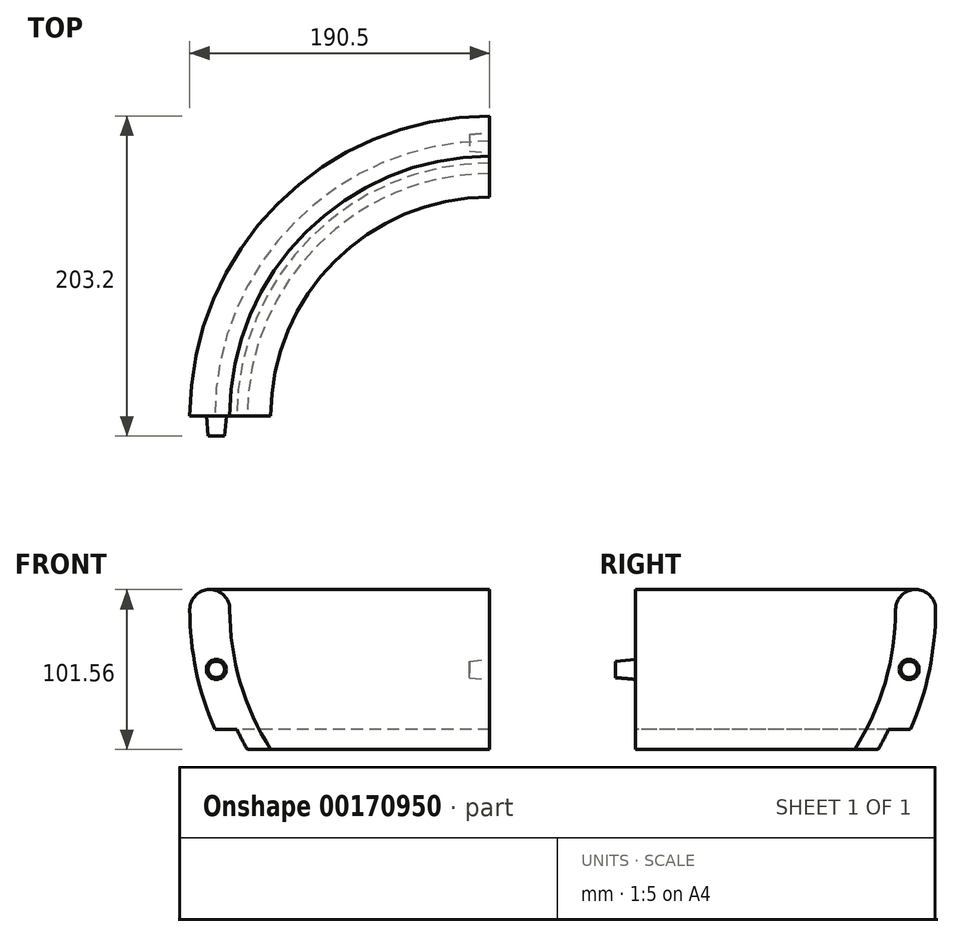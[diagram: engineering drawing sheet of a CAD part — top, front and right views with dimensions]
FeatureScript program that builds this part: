
annotation { "Feature Type Name" : "Feature", "Feature Type Description" : "" }
export const myFeature = defineFeature(function(context is Context, id is Id, definition is map)
    precondition{}
    {
        {
            var Q0;
            Q0=qCreatedBy(makeId("Front.planeOp"),FACE);
            var sketch = newSketch(context, id + "F0", { "sketchPlane" : qUnion([Q0])});
            skLineSegment(sketch, "E0", {"start": v(0, 0) * mm, "end": v(-165.1, 0) * mm});
            skLineSegment(sketch, "E1", {"start": v(0, 0) * mm, "end": v(0, -76.2) * mm});
            skLineSegment(sketch, "E2", {"start": v(0, -76.2) * mm, "end": v(-160.64, -76.2) * mm});
            skArc(sketch, "E3", {"start": v(-177.35, -12.7) * mm, "mid": v(-171.94, -45.26) * mm, "end": v(-160.62, -76.26) * mm});
            skArc(sketch, "E4", {"start": v(-190.5, 0) * mm, "mid": v(-186.48, -38.92) * mm, "end": v(-174.6, -76.2) * mm});
            skArc(sketch, "E5", {"start": v(-160.62, -76.26) * mm, "mid": v(-157.43, -82.64) * mm, "end": v(-153.98, -88.9) * mm});
            skArc(sketch, "E6", {"start": v(-165.1, 0) * mm, "mid": v(-158.47, -46.3) * mm, "end": v(-139.12, -88.9) * mm});
            skLineSegment(sketch, "E7", {"start": v(-177.35, 12.7) * mm, "end": v(-177.35, 12.7) * mm});
            skArc(sketch, "E8", {"start": v(-177.35, 12.7) * mm, "mid": v(-177.35, 12.67) * mm, "end": v(-177.35, 12.65) * mm});
            skLineSegment(sketch, "E9", {"start": v(-165.1, 0) * mm, "end": v(-177.7, 0) * mm});
            skLineSegment(sketch, "E10", {"start": v(-153.98, -88.9) * mm, "end": v(-139.12, -88.9) * mm});
            skLineSegment(sketch, "E11", {"start": v(-174.6, -76.2) * mm, "end": v(-160.62, -76.26) * mm});
            skLineSegment(sketch, "E12", {"start": v(-177.7, 0) * mm, "end": v(-177.8, 0) * mm});
            skArc(sketch, "E13", {"start": v(-165.1, 0) * mm, "mid": v(-177.8, 12.66) * mm, "end": v(-190.5, 0) * mm});
            skArc(sketch, "E14.trimOffspring", {"start": v(-177.8, 0) * mm, "mid": v(-177.69, -6.36) * mm, "end": v(-177.35, -12.7) * mm});
            skSolve(sketch);
        }
        {
            var Q0;
            Q0=makeQuery(id+"F0.imprint","IMPRINT",FACE,{"disambiguationData":[TD([[makeQuery(id+"F0.imprint","IMPRINT",EDGE,{"derivedFrom":sQuery(id+"F0.wireOp",EDGE,"E4")}),1.0]])]});
            var Q1;
            {var subQ4=sQuery(id+"F0.wireOp",EDGE,"E9");Q1=makeQuery(id+"F0.imprint","IMPRINT",FACE,{"disambiguationData":[TD([[makeQuery(id+"F0.imprint","IMPRINT",EDGE,{"derivedFrom":subQ4}),1.0]])]});}
            var Q2;
            {var subQ4=sQuery(id+"F0.wireOp",EDGE,"E5");Q2=makeQuery(id+"F0.imprint","IMPRINT",FACE,{"disambiguationData":[TD([[makeQuery(id+"F0.imprint","IMPRINT",EDGE,{"derivedFrom":subQ4}),1.0]])]});}
            var Q3;
            Q3=sQuery(id+"F0.wireOp",EDGE,"E1");
            revolve(context, id + "F1", {"entities" : qUnion([Q0, Q1, Q2]), "axis" : qUnion([Q3]), "revolveType" : RevolveType.ONE_DIRECTION, "angle" : 90 * degree});
        }
        {
            var Q0;
            Q0=makeQuery(id+"F0.imprint","IMPRINT",FACE,{"disambiguationData":[TD([[makeQuery(id+"F0.imprint","IMPRINT",EDGE,{"derivedFrom":sQuery(id+"F0.wireOp",EDGE,"E4")}),1.0]])]});
            var sketch = newSketch(context, id + "F2", { "sketchPlane" : qUnion([Q0])});
            skCircle(sketch, "E15", {"center": v(-173.67, -38.1) * mm, "radius": 6.35 * mm});
            skSolve(sketch);
        }
        {
            var Q0;
            Q0=qSketchRegion(id+"F2",true);
            extrude(context, id + "F3", {"entities" : qUnion([Q0]), "operationType" : NewBodyOperationType.ADD, "depth" : 12.7 * mm, "hasDraft" : true, "draftAngle" : 5 * degree, "draftPullDirection" : true});
        }
        {
            var Q0;
            Q0=makeQuery(id+"F1.opRevolve","CAP_FACE",FACE,{"disambiguationData":[OSD([sQuery(id+"F0.wireOp",EDGE,"E4"),sQuery(id+"F0.wireOp",EDGE,"E5"),sQuery(id+"F0.wireOp",EDGE,"E6"),sQuery(id+"F0.wireOp",EDGE,"E8"),sQuery(id+"F0.wireOp",EDGE,"E9"),sQuery(id+"F0.wireOp",EDGE,"IzXMlpwB-L7sk-yMcw-xoRI-lU3HIr0pnRP3"),sQuery(id+"F0.wireOp",EDGE,"E10"),sQuery(id+"F0.wireOp",EDGE,"E11"),sQuery(id+"F0.wireOp",EDGE,"E12")])],"isStart":false});
            var sketch = newSketch(context, id + "F4", { "sketchPlane" : qUnion([Q0])});
            skCircle(sketch, "E16", {"center": v(173.67, -38.1) * mm, "radius": 6.35 * mm});
            skSolve(sketch);
        }
        {
            var Q0;
            Q0=qSketchRegion(id+"F4",true);
            extrude(context, id + "F5", {"entities" : qUnion([Q0]), "operationType" : NewBodyOperationType.REMOVE, "oppositeDirection" : true, "depth" : 12.7 * mm, "hasDraft" : true, "draftAngle" : 5 * degree, "draftPullDirection" : true});
        }
    });
